# Revit family: Zumtobel INT M LC
name_source: partatom
category: Lighting Fixtures
revit_build: Autodesk Revit 2016 (Build: 20150220_1215(x64)
units: mm (PartAtom-declared; Revit-internal decimal feet)

## family parameters
Cut with Voids When Loaded = No
Host = Face
Light Source = Yes
OmniClass Number = 23.80.70.11
OmniClass Title = Luminaries for Internal Lighting
Part Type = Normal
Room Calculation Point = No
Round Connector Dimension = Use Diameter
Shared = No

## types (1)
- INT M LC
    Apparent Load = 43 VA
    Assembly Code = D5020200
    Body = ZG_Metal_White
    Color Filter = 16777215
    Default Elevation = 0 mm  [stored 0 ft]
    Depth = 98 mm  [stored 0.321522 ft]
    Description = Ceiling recressed LED luminaire
    Dimming Lamp Color Temperature Shift = <None>
    Emit Shape Visible in Rendering = No
    Emit from Circle Diameter = 110 mm  [stored 0.360892 ft]
    Height = 180 mm  [stored 0.590551 ft]
    Manufacturer = Zumtobel Lighting
    Model = 60210784
    Photometric Web File = 60210784_(STD_LEO).IES
    Reflector = ZG_Self_llumination_Opaque
    Tilt Angle = 90.00°
    URL = http://www.zumtobel.com
    Voltage = 0 V
    Width = 180 mm  [stored 0.590551 ft]

note: [stored X ft] marks values corroborated as IEEE doubles in the binary element streams (Revit-internal decimal feet)

## geometry (parser evidence)
native form markers: Blend x2, Sweep x2
no freeform markers — native parametric forms only
